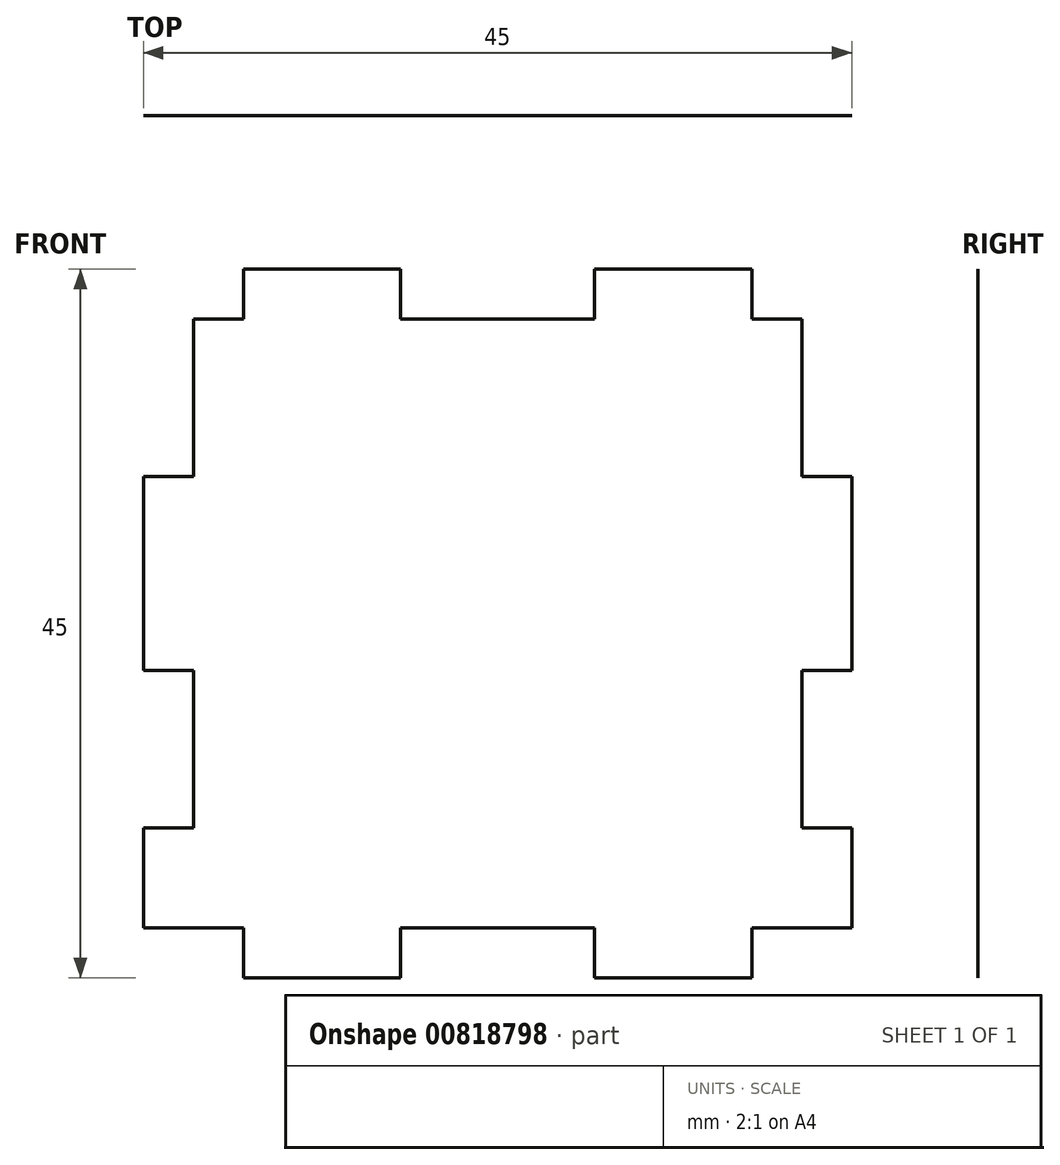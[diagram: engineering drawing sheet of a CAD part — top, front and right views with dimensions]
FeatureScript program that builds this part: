
annotation { "Feature Type Name" : "Feature", "Feature Type Description" : "" }
export const myFeature = defineFeature(function(context is Context, id is Id, definition is map)
    precondition{}
    {
        {
            var Q0;
            Q0=qCreatedBy(makeId("Front.planeOp"),FACE);
            var sketch = newSketch(context, id + "F0", { "sketchPlane" : qUnion([Q0])});
            skPoint(sketch, "E0.middle", {"position": v(0, 0) * mm});
            skLineSegment(sketch, "E1", {"start": v(-22.5, -22.5) * mm, "end": v(-16.15, -22.5) * mm});
            skLineSegment(sketch, "E2", {"start": v(-16.15, -25.67) * mm, "end": v(-16.15, -22.5) * mm});
            skLineSegment(sketch, "E3", {"start": v(-16.15, -25.67) * mm, "end": v(-6.15, -25.67) * mm});
            skLineSegment(sketch, "E4", {"start": v(-6.15, -22.5) * mm, "end": v(-6.15, -25.67) * mm});
            skLineSegment(sketch, "E5", {"start": v(-6.15, -22.5) * mm, "end": v(6.15, -22.5) * mm});
            skLineSegment(sketch, "E6", {"start": v(6.15, -25.67) * mm, "end": v(6.15, -22.5) * mm});
            skLineSegment(sketch, "E7", {"start": v(6.15, -25.67) * mm, "end": v(16.15, -25.67) * mm});
            skLineSegment(sketch, "E8", {"start": v(16.15, -22.5) * mm, "end": v(16.15, -25.68) * mm});
            skLineSegment(sketch, "E9", {"start": v(16.15, -22.5) * mm, "end": v(22.5, -22.5) * mm});
            skPoint(sketch, "E10", {"position": v(0, -22.5) * mm});
            skLineSegment(sketch, "E11.bottom", {"start": v(-22.5, 16.15) * mm, "end": v(-19.33, 16.15) * mm});
            skLineSegment(sketch, "E11.top", {"start": v(-22.5, 6.15) * mm, "end": v(-19.33, 6.15) * mm});
            skLineSegment(sketch, "E11.left", {"start": v(-22.5, 16.15) * mm, "end": v(-22.5, 6.15) * mm});
            skLineSegment(sketch, "E11.right", {"start": v(-19.33, 16.15) * mm, "end": v(-19.33, 6.15) * mm});
            skLineSegment(sketch, "E12.bottom", {"start": v(-22.5, -6.15) * mm, "end": v(-19.33, -6.15) * mm});
            skLineSegment(sketch, "E12.top", {"start": v(-22.5, -16.15) * mm, "end": v(-19.33, -16.15) * mm});
            skLineSegment(sketch, "E12.left", {"start": v(-22.5, -6.15) * mm, "end": v(-22.5, -16.15) * mm});
            skLineSegment(sketch, "E12.right", {"start": v(-19.33, -6.15) * mm, "end": v(-19.33, -16.15) * mm});
            skLineSegment(sketch, "E13.top", {"start": v(22.5, 6.15) * mm, "end": v(19.32, 6.15) * mm});
            skLineSegment(sketch, "E13.left", {"start": v(22.5, 16.15) * mm, "end": v(22.5, 6.15) * mm});
            skLineSegment(sketch, "E13.right", {"start": v(19.32, 16.15) * mm, "end": v(19.32, 6.15) * mm});
            skLineSegment(sketch, "E14.bottom", {"start": v(22.5, -6.15) * mm, "end": v(19.32, -6.15) * mm});
            skLineSegment(sketch, "E14.top", {"start": v(22.5, -16.15) * mm, "end": v(19.32, -16.15) * mm});
            skLineSegment(sketch, "E14.left", {"start": v(22.5, -6.15) * mm, "end": v(22.5, -16.15) * mm});
            skLineSegment(sketch, "E14.right", {"start": v(19.32, -6.15) * mm, "end": v(19.32, -16.15) * mm});
            skLineSegment(sketch, "E15", {"start": v(-20.91, 6.15) * mm, "end": v(-20.91, -6.15) * mm});
            skLineSegment(sketch, "E16", {"start": v(20.91, 6.15) * mm, "end": v(20.91, -6.15) * mm});
            skPoint(sketch, "E17", {"position": v(-20.91, 0) * mm});
            skPoint(sketch, "E18", {"position": v(20.91, 0) * mm});
            skLineSegment(sketch, "E19", {"start": v(22.5, -16.15) * mm, "end": v(22.5, -22.5) * mm});
            skLineSegment(sketch, "E20", {"start": v(22.5, 6.15) * mm, "end": v(22.5, -6.15) * mm});
            skLineSegment(sketch, "E21", {"start": v(19.32, 16.15) * mm, "end": v(22.5, 16.15) * mm});
            skLineSegment(sketch, "E22", {"start": v(19.32, 16.15) * mm, "end": v(16.15, 16.15) * mm});
            skLineSegment(sketch, "E23", {"start": v(16.15, 16.15) * mm, "end": v(16.15, 19.32) * mm});
            skLineSegment(sketch, "E24", {"start": v(16.15, 19.33) * mm, "end": v(6.15, 19.33) * mm});
            skLineSegment(sketch, "E25", {"start": v(6.15, 19.33) * mm, "end": v(6.15, 16.15) * mm});
            skLineSegment(sketch, "E26", {"start": v(6.15, 16.15) * mm, "end": v(-6.15, 16.15) * mm});
            skLineSegment(sketch, "E27", {"start": v(-6.15, 16.15) * mm, "end": v(-6.15, 19.33) * mm});
            skLineSegment(sketch, "E28", {"start": v(-6.15, 19.33) * mm, "end": v(-16.15, 19.33) * mm});
            skLineSegment(sketch, "E29", {"start": v(-16.15, 19.33) * mm, "end": v(-16.15, 16.15) * mm});
            skLineSegment(sketch, "E30", {"start": v(-16.15, 16.15) * mm, "end": v(-19.33, 16.15) * mm});
            skLineSegment(sketch, "E31", {"start": v(-22.5, 6.15) * mm, "end": v(-22.5, -6.15) * mm});
            skLineSegment(sketch, "E32", {"start": v(-22.5, -16.15) * mm, "end": v(-22.5, -22.5) * mm});
            skSolve(sketch);
        }
        {
            var Q0;
            {var subQ5=sQuery(id+"F0.wireOp",EDGE,"VL84kJ3D-u9bM-tbnH-1Cpo-V7k9Bp2refEE");Q0=makeQuery(id+"F0.imprint","IMPRINT",FACE,{"disambiguationData":[TD([[makeQuery(id+"F0.imprint","IMPRINT",EDGE,{"derivedFrom":subQ5}),1.0]])]});}
            var Q1;
            {var subQ5=sQuery(id+"F0.wireOp",EDGE,"E16");Q1=makeQuery(id+"F0.imprint","IMPRINT",FACE,{"disambiguationData":[TD([[makeQuery(id+"F0.imprint","IMPRINT",EDGE,{"derivedFrom":subQ5}),1.0]])]});}
            var Q2;
            {var subQ5=sQuery(id+"F0.wireOp",EDGE,"E15");Q2=makeQuery(id+"F0.imprint","IMPRINT",FACE,{"disambiguationData":[TD([[makeQuery(id+"F0.imprint","IMPRINT",EDGE,{"derivedFrom":subQ5}),-1.0]])]});}
            var Q3;
            {var subQ19=sQuery(id+"F0.wireOp",EDGE,"E1");Q3=makeQuery(id+"F0.imprint","IMPRINT",FACE,{"disambiguationData":[TD([[makeQuery(id+"F0.imprint","IMPRINT",EDGE,{"derivedFrom":subQ19}),1.0]])]});}
            extrude(context, id + "F1", {"entities" : qUnion([Q0, Q1, Q2, Q3]), "depth" : 1 / 203.2 * mm, "offsetDistance" : 25 * mm});
        }
    });
